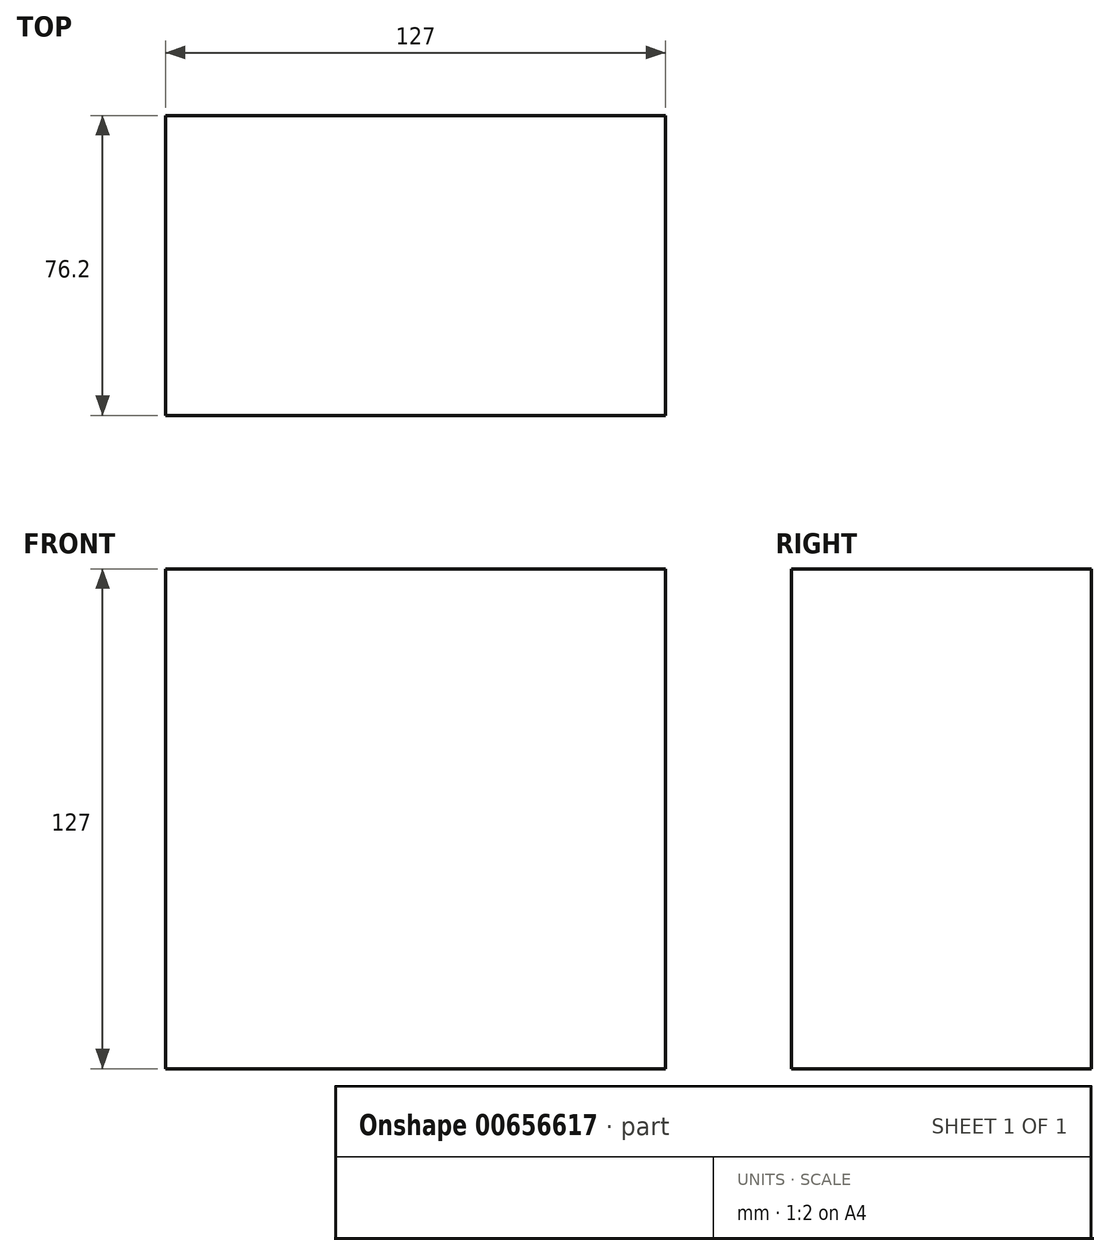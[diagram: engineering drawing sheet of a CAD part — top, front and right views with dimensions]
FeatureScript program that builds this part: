
annotation { "Feature Type Name" : "Feature", "Feature Type Description" : "" }
export const myFeature = defineFeature(function(context is Context, id is Id, definition is map)
    precondition{}
    {
        {
            var Q0;
            Q0=qCreatedBy(makeId("Front.planeOp"),FACE);
            var sketch = newSketch(context, id + "F0", { "sketchPlane" : qUnion([Q0])});
            skLineSegment(sketch, "E0.bottom", {"start": v(-63.5, 63.5) * mm, "end": v(63.5, 63.5) * mm});
            skLineSegment(sketch, "E0.top", {"start": v(-63.5, -63.5) * mm, "end": v(63.5, -63.5) * mm});
            skLineSegment(sketch, "E0.left", {"start": v(-63.5, 63.5) * mm, "end": v(-63.5, -63.5) * mm});
            skLineSegment(sketch, "E0.right", {"start": v(63.5, 63.5) * mm, "end": v(63.5, -63.5) * mm});
            skSolve(sketch);
        }
        {
            var Q0;
            Q0 = qSketchRegion(id + "F0", true);
            extrude(context, id + "F1", {"entities" : qUnion([Q0]), "endBound" : BoundingType.SYMMETRIC, "oppositeDirection" : true, "depth" : 76.2 * mm, "offsetDistance" : 25.4 * mm});
        }
    });
